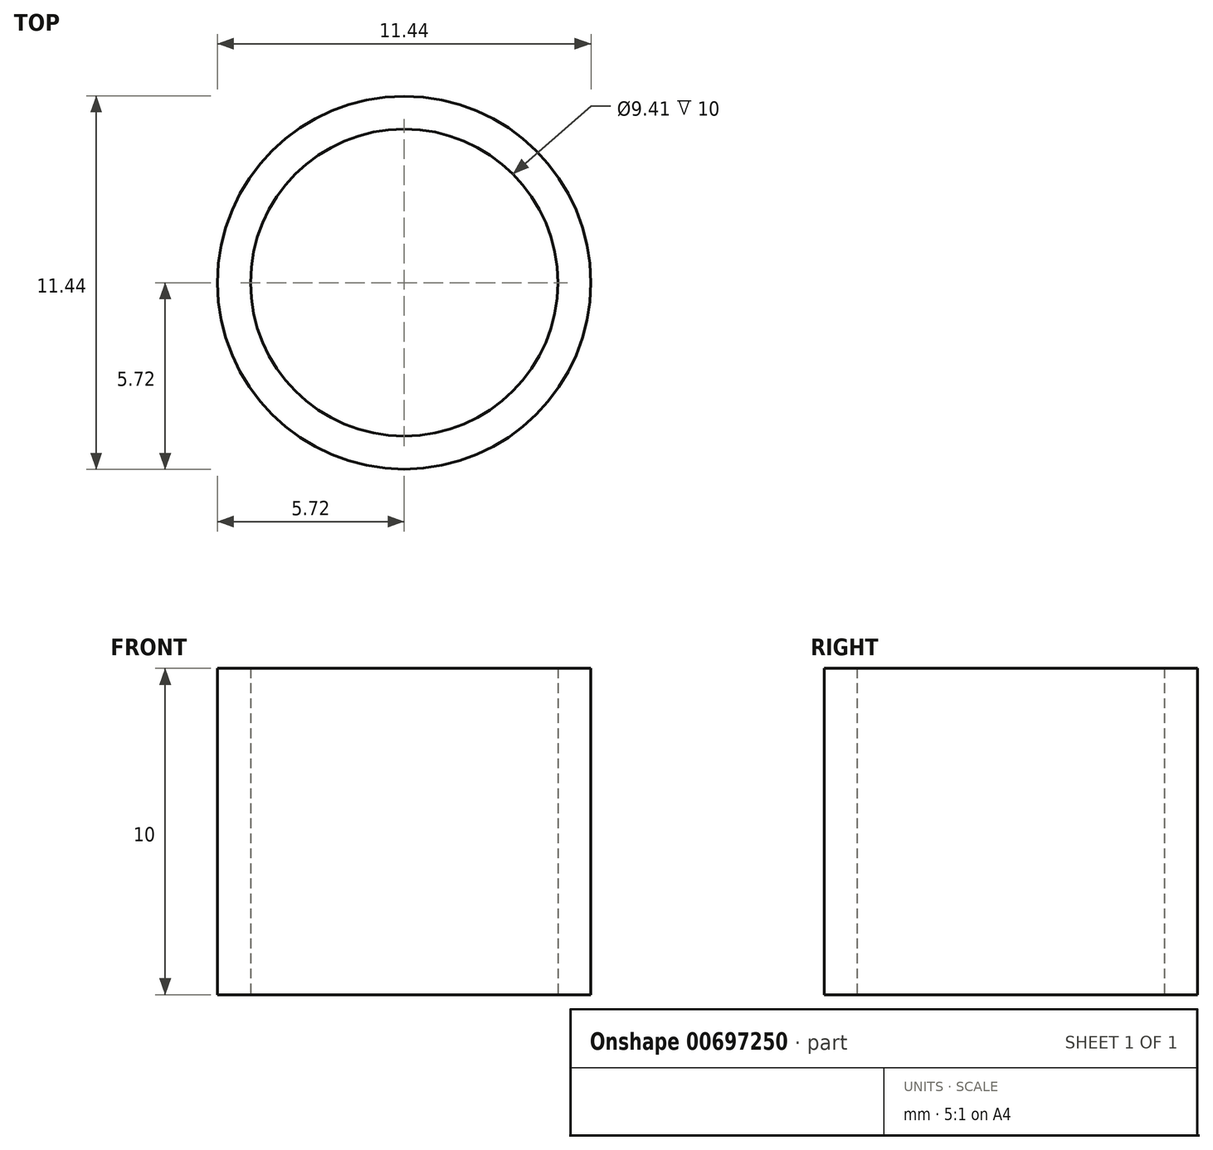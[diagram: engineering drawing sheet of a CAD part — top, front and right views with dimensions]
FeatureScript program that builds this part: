
annotation { "Feature Type Name" : "Feature", "Feature Type Description" : "" }
export const myFeature = defineFeature(function(context is Context, id is Id, definition is map)
    precondition{}
    {
        {
            var Q0;
            Q0=qCreatedBy(makeId("Top.planeOp"),FACE);
            var sketch = newSketch(context, id + "F0", { "sketchPlane" : qUnion([Q0])});
            skCircle(sketch, "E0", {"center": v(0, 0) * mm, "radius": 4.7 * mm});
            skCircle(sketch, "E1", {"center": v(0, 0) * mm, "radius": 5.71 * mm});
            skSolve(sketch);
        }
        {
            var Q0;
            Q0=makeQuery(id+"F0.imprint","IMPRINT",FACE,{"disambiguationData":[TD([[makeQuery(id+"F0.imprint","IMPRINT",EDGE,{"derivedFrom":sQuery(id+"F0.wireOp",EDGE,"E0")}),-1.0]])]});
            extrude(context, id + "F1", {"entities" : qUnion([Q0]), "depth" : 10 * mm, "offsetDistance" : 25 * mm});
        }
    });
